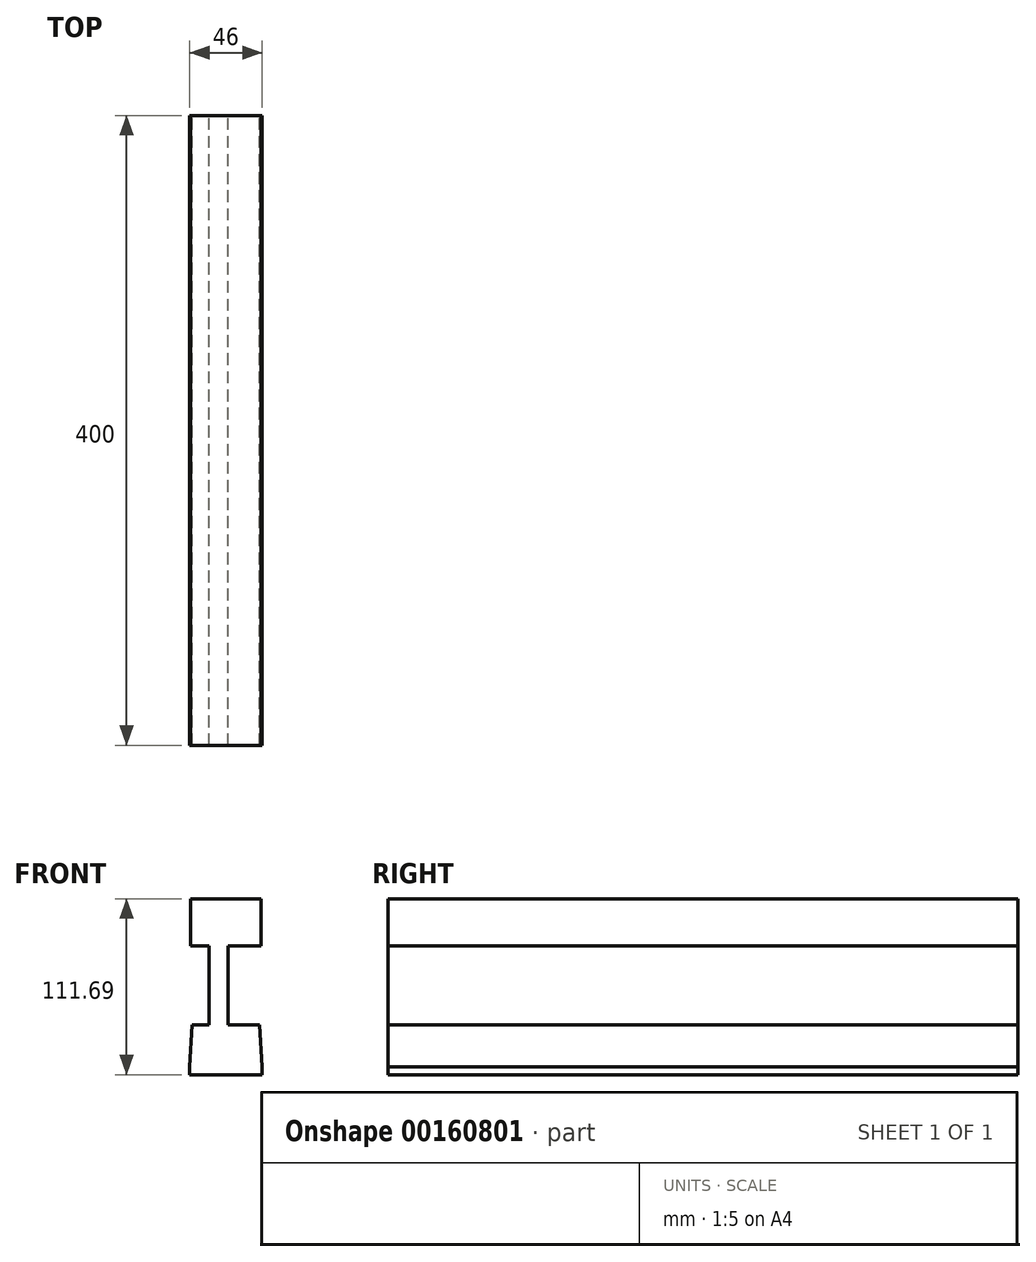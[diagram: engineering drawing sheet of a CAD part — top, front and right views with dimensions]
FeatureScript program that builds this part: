
annotation { "Feature Type Name" : "Feature", "Feature Type Description" : "" }
export const myFeature = defineFeature(function(context is Context, id is Id, definition is map)
    precondition{}
    {
        {
            var Q0;
            Q0=qCreatedBy(makeId("Front.planeOp"),FACE);
            var sketch = newSketch(context, id + "F0", { "sketchPlane" : qUnion([Q0])});
            skLineSegment(sketch, "E0", {"start": v(-46.71, 53.06) * mm, "end": v(-58.71, 53.06) * mm});
            skLineSegment(sketch, "E1", {"start": v(-58.71, 53.06) * mm, "end": v(-58.71, 83.06) * mm});
            skLineSegment(sketch, "E2", {"start": v(-58.71, 83.06) * mm, "end": v(-13.71, 83.06) * mm});
            skLineSegment(sketch, "E3", {"start": v(-13.71, 83.06) * mm, "end": v(-13.71, 53.06) * mm});
            skLineSegment(sketch, "E4", {"start": v(-13.71, 53.06) * mm, "end": v(-34.71, 53.06) * mm});
            skLineSegment(sketch, "E5", {"start": v(-34.71, 53.06) * mm, "end": v(-34.71, 3.06) * mm});
            skLineSegment(sketch, "E6", {"start": v(-34.71, 3.06) * mm, "end": v(-14.71, 3.06) * mm});
            skLineSegment(sketch, "E7", {"start": v(-34.71, -28.63) * mm, "end": v(-13.21, -28.63) * mm});
            skLineSegment(sketch, "E8", {"start": v(-34.71, -28.63) * mm, "end": v(-59.21, -28.63) * mm});
            skLineSegment(sketch, "E9", {"start": v(-59.21, -28.63) * mm, "end": v(-59.21, -23.63) * mm});
            skLineSegment(sketch, "E10", {"start": v(-46.71, 53.06) * mm, "end": v(-46.71, 3.06) * mm});
            skLineSegment(sketch, "E11", {"start": v(-46.71, 3.06) * mm, "end": v(-57.71, 3.06) * mm});
            skLineSegment(sketch, "E12", {"start": v(-57.71, 3.06) * mm, "end": v(-59.21, -23.63) * mm});
            skLineSegment(sketch, "E13", {"start": v(-13.21, -28.63) * mm, "end": v(-13.21, -23.63) * mm});
            skLineSegment(sketch, "E14", {"start": v(-13.21, -23.63) * mm, "end": v(-14.71, 3.06) * mm});
            skSolve(sketch);
        }
        {
            var Q0;
            Q0=makeQuery(id+"F0.imprint","IMPRINT",FACE,{"disambiguationData":[TD([[makeQuery(id+"F0.imprint","IMPRINT",EDGE,{"derivedFrom":sQuery(id+"F0.wireOp",EDGE,"E0")}),-1.0]])]});
            extrude(context, id + "F1", {"entities" : qUnion([Q0]), "depth" : 400 * mm});
        }
    });
